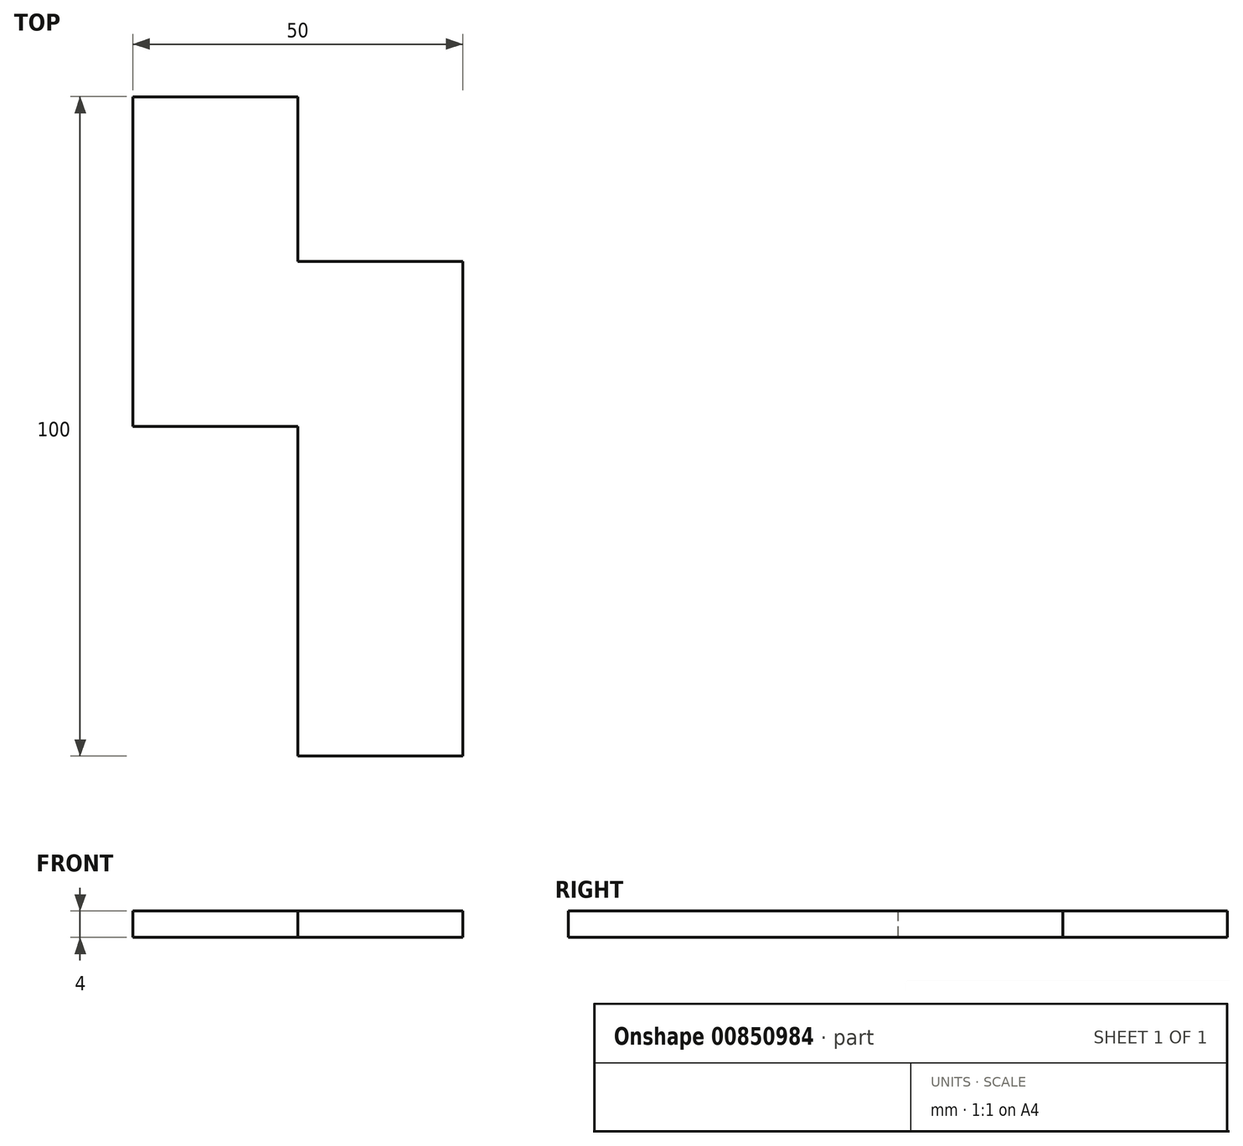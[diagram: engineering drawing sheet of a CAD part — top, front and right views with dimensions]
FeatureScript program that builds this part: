
annotation { "Feature Type Name" : "Feature", "Feature Type Description" : "" }
export const myFeature = defineFeature(function(context is Context, id is Id, definition is map)
    precondition{}
    {
        {
            var Q0;
            Q0=qCreatedBy(makeId("Top.planeOp"),FACE);
            var sketch = newSketch(context, id + "F0", { "sketchPlane" : qUnion([Q0])});
            skLineSegment(sketch, "E0", {"start": v(-49.09, 33.88) * mm, "end": v(65.16, 33.88) * mm, "construction": true});
            skLineSegment(sketch, "E1", {"start": v(-41.33, -16.12) * mm, "end": v(95.2, -16.12) * mm, "construction": true});
            skLineSegment(sketch, "E2", {"start": v(-50.07, 8.88) * mm, "end": v(107.88, 8.88) * mm, "construction": true});
            skLineSegment(sketch, "E3", {"start": v(37.45, 51.41) * mm, "end": v(37.45, -77.62) * mm, "construction": true});
            skLineSegment(sketch, "E4", {"start": v(62.45, 45.95) * mm, "end": v(62.45, -66.12) * mm, "construction": true});
            skLineSegment(sketch, "E5", {"start": v(12.45, 48.35) * mm, "end": v(12.45, -75.08) * mm, "construction": true});
            skLineSegment(sketch, "E6", {"start": v(-75.2, -66.12) * mm, "end": v(138.24, -66.12) * mm, "construction": true});
            skSolve(sketch);
        }
        {
            var Q0;
            Q0=qCreatedBy(makeId("Top.planeOp"),FACE);
            var sketch = newSketch(context, id + "F1", { "sketchPlane" : qUnion([Q0])});
            skLineSegment(sketch, "E7.0", {"start": v(-50.07, 8.88) * mm, "end": v(107.88, 8.88) * mm, "construction": true});
            skLineSegment(sketch, "E7.1", {"start": v(37.45, 51.41) * mm, "end": v(37.45, -77.62) * mm, "construction": true});
            skLineSegment(sketch, "E7.2", {"start": v(12.45, 48.35) * mm, "end": v(12.45, -75.08) * mm, "construction": true});
            skLineSegment(sketch, "E7.3", {"start": v(-49.09, 33.88) * mm, "end": v(65.16, 33.88) * mm, "construction": true});
            skLineSegment(sketch, "E7.4", {"start": v(62.45, 45.95) * mm, "end": v(62.45, -66.12) * mm, "construction": true});
            skLineSegment(sketch, "E7.5", {"start": v(-41.33, -16.12) * mm, "end": v(95.2, -16.12) * mm, "construction": true});
            skLineSegment(sketch, "E7.6", {"start": v(-75.2, -66.12) * mm, "end": v(138.24, -66.12) * mm, "construction": true});
            skLineSegment(sketch, "E8", {"start": v(12.45, 33.88) * mm, "end": v(37.45, 33.88) * mm});
            skLineSegment(sketch, "E9", {"start": v(37.45, 33.88) * mm, "end": v(37.45, 8.88) * mm});
            skLineSegment(sketch, "E10", {"start": v(37.45, 8.88) * mm, "end": v(62.45, 8.88) * mm});
            skLineSegment(sketch, "E11", {"start": v(62.45, 8.88) * mm, "end": v(62.45, -66.12) * mm});
            skLineSegment(sketch, "E12", {"start": v(37.45, -66.12) * mm, "end": v(37.45, -16.12) * mm});
            skLineSegment(sketch, "E13", {"start": v(37.45, -16.12) * mm, "end": v(12.45, -16.12) * mm});
            skLineSegment(sketch, "E14", {"start": v(12.45, -16.12) * mm, "end": v(12.45, 33.88) * mm});
            skLineSegment(sketch, "E15", {"start": v(37.45, -66.12) * mm, "end": v(62.45, -66.12) * mm});
            skSolve(sketch);
        }
        {
            var Q0;
            Q0 = qSketchRegion(id + "F1", true);
            extrude(context, id + "F2", {"entities" : qUnion([Q0]), "depth" : 4 * mm, "offsetDistance" : 25 * mm});
        }
    });
